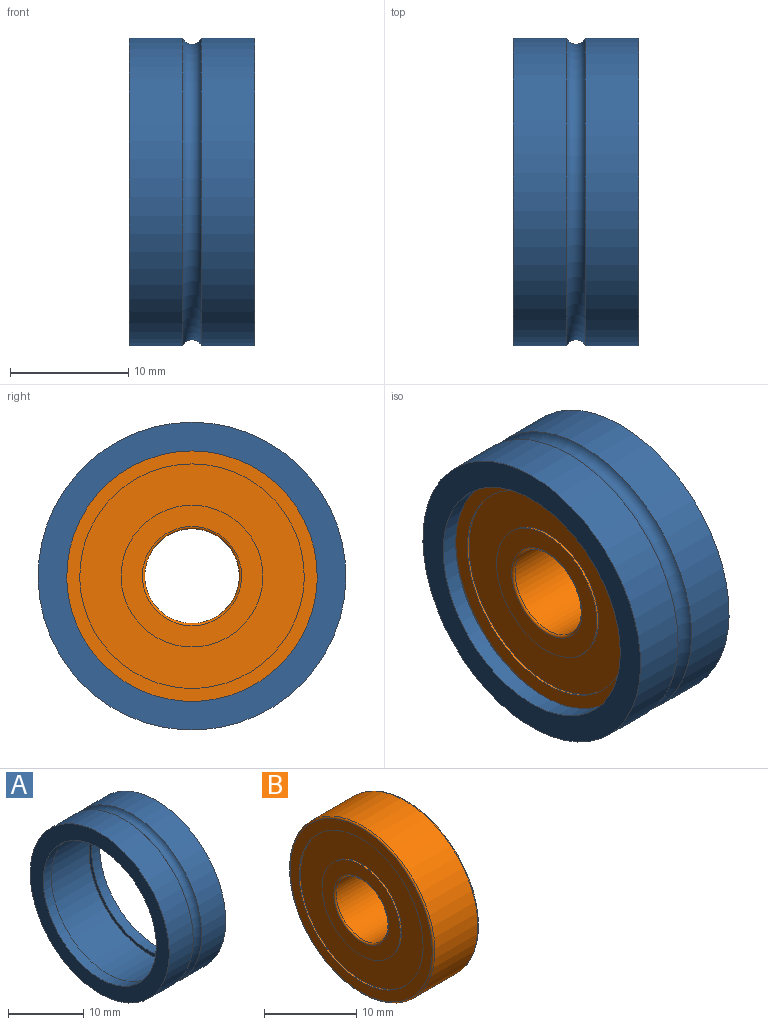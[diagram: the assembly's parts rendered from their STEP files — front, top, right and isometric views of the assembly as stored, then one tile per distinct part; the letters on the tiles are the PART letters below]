
ASSEMBLY  parts=2 mates=1
PART A: 10 faces, bbox 10.6x29x29 mm
  f0: cylinder r=13.03mm len=26.05mm, axis (-1,0,0), area 368.1mm2, adj f1,f9
  f1: plane 26.05x26.05mm, normal (-1,0,0), area 180mm2, adj f0,f2
  f2: cylinder r=10.6mm len=21.2mm, axis (-1,0,0), area 99.9mm2, adj f1,f3
  f3: plane 22.2x22.2mm, normal (1,0,0), area 34.1mm2, adj f2,f4
  f4: cylinder r=11.1mm len=22.2mm, axis (-1,0,0), area 530mm2, adj f3,f5
  f5: plane 22.2x22.2mm, normal (-1,0,0), area 34.1mm2, adj f4,f6
  f6: cylinder r=10.6mm len=21.2mm, axis (-1,0,0), area 99.9mm2, adj f5,f7
  f7: plane 26.05x26.05mm, normal (1,0,0), area 180mm2, adj f6,f8
  f8: cylinder r=13.03mm len=26.05mm, axis (-1,0,0), area 368.1mm2, adj f7,f9
  f9: torus R=13.38mm, axis (-1,0,0), area 161.7mm2, adj f0,f8
PART B: 16 faces, bbox 7x24x24 mm
  f0: plane 12x12mm, normal (-1,0,0), area 57.7mm2, adj f7,f13
  f1: plane 12x12mm, normal (1,0,0), area 57.7mm2, adj f8,f10
  f2: cylinder r=11.1mm len=22.2mm, axis (-1,0,0), area 460.3mm2, adj f6,f9
  f3: plane 21.8x21.8mm, normal (-1,0,0), area 89.7mm2, adj f6,f14
  f4: cylinder r=4mm len=8mm, axis (-1,0,0), area 165.9mm2, adj f7,f8
  f5: plane 21.8x21.8mm, normal (1,0,0), area 89.7mm2, adj f9,f11
  f6: torus R=10.9mm, axis (1,0,0), area 21.8mm2, adj f2,f3
  f7: torus R=4.2mm, axis (1,0,0), area 8mm2, adj f0,f4
  f8: torus R=4.2mm, axis (1,0,0), area 8mm2, adj f1,f4
  f9: torus R=10.9mm, axis (1,0,0), area 21.8mm2, adj f2,f5
  f10: cylinder r=6mm len=12mm, axis (1,0,0), area 7.5mm2, adj f1,f12
  f11: cylinder r=9.5mm len=19mm, axis (1,0,0), area 11.9mm2, adj f5,f12
  f12: plane 19x19mm, normal (1,0,0), area 170.4mm2, adj f10,f11
  f13: cylinder r=6mm len=12mm, axis (-1,0,0), area 7.5mm2, adj f0,f15
  f14: cylinder r=9.5mm len=19mm, axis (-1,0,0), area 11.9mm2, adj f3,f15
  f15: plane 19x19mm, normal (-1,0,0), area 170.4mm2, adj f13,f14
PLACE A t=(-5.41,-0.09,0.16)mm
PLACE B t=(-5.41,-0.09,0.16)mm
MATE fastened B.f2 <-> A.f0  axis (-1,0,0) through (-8.71,-0.09,0.16)mm
